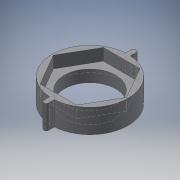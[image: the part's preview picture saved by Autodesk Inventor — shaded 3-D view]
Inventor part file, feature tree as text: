
AUTODESK INVENTOR PART (.ipt)
format: ipt  version: 2017 (Build 210142000, 142)  size: 142,336 bytes
history: native  units: mm
features: other x3, extrude x2, sketch x2, hole x1, direct_edit x1, reference x1, move_body x1
ambient origin geometry x8: Origin, YZ Plane, XZ Plane, XY Plane, X Axis, Y Axis, Z Axis, Center Point
bodies: Solid1 (feature_tree)
feature tree (11):
  extrude  "Extrusion1"  Depth=0.25mm
  extrude  "Extrusion2"  Depth=8.0mm
  hole  "Hole1"  [1 undecoded]
  direct_edit  "Direct Edit1"
  sketch  "Sketch1"  dims[d2=0.2mm d3=0.25mm]
  sketch  "Sketch2"  dims[d4=3.0mm d5=0.0mm d6=8.0mm d7=1.0mm d8=0.0mm d9=10.0mm d10=10.0mm d11=6.5mm d12=6.0mm d13=4.0mm d14=2.0mm d15=90.0deg d16=8.0mm d17=20.594885mm d18=0.0mm d19=0.0mm d20=-0.5mm]
  reference  "Reference9"
  parser-record x1  (decoder bookkeeping rows leaked as tree rows — omitted from the tree; the rows remain in map.json)
  other  "assembly_full.iam"
  other  "base:1"
  move_body  "Move1"
note: 1 required parameter value undecoded (feature->parameter linkage not recoverable at this tier; creation-order binding heuristic only, values carry confidence <= 0.55)
note: 1 file-system path scrubbed to <path> (originals preserved in map.json)
